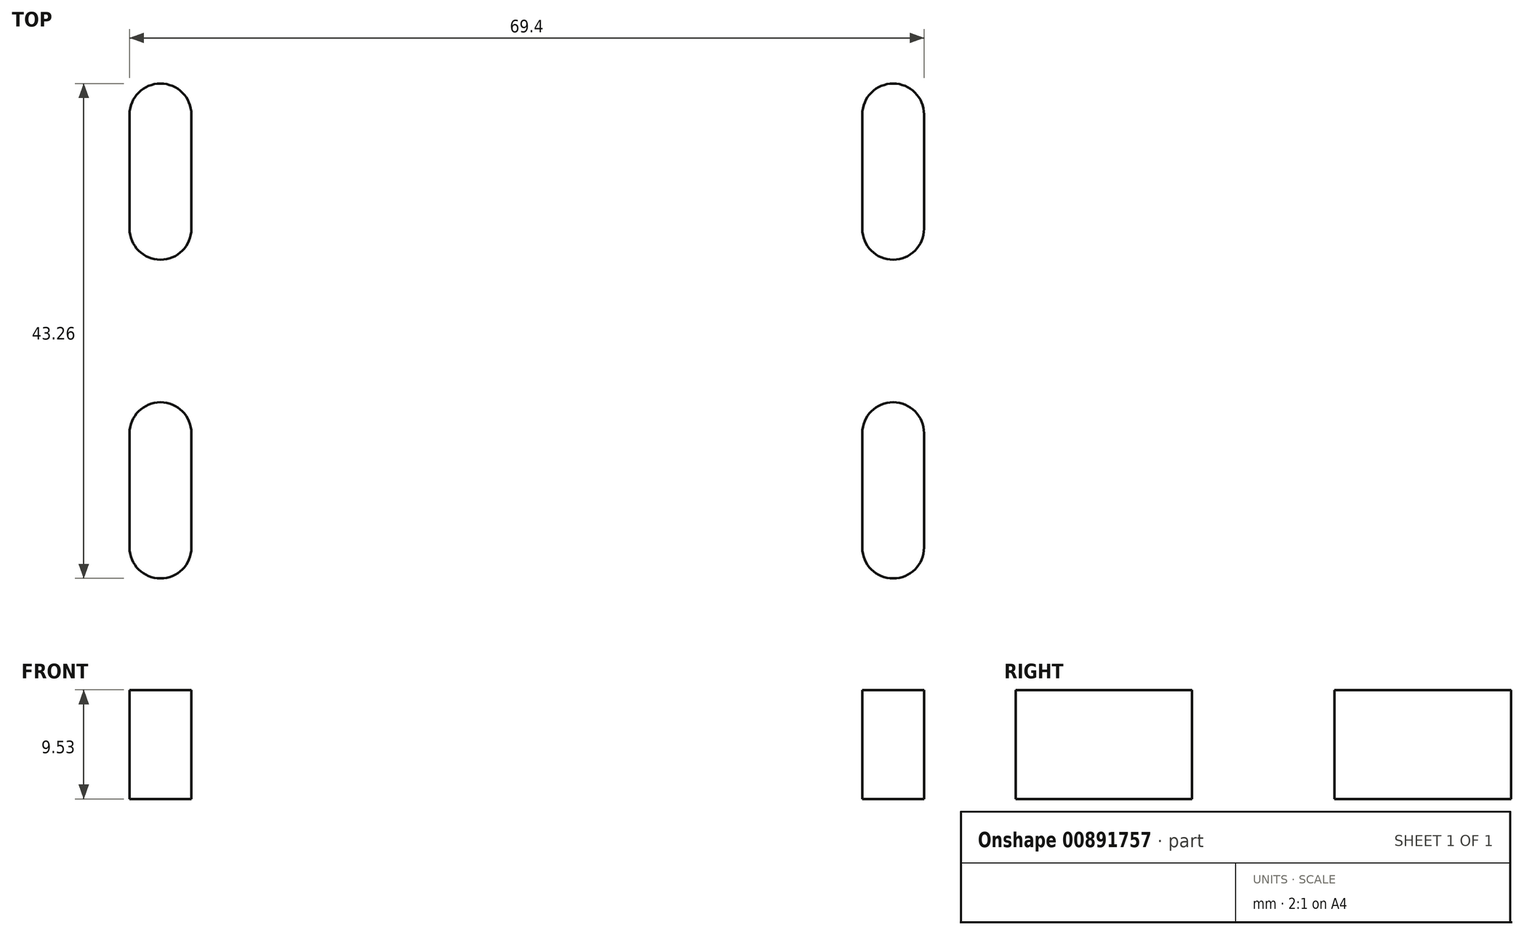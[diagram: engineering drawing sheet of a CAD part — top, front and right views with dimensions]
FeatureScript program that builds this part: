
annotation { "Feature Type Name" : "Feature", "Feature Type Description" : "" }
export const myFeature = defineFeature(function(context is Context, id is Id, definition is map)
    precondition{}
    {
        {
            var Q0;
            Q0=qCreatedBy(makeId("Top.planeOp"),FACE);
            var sketch = newSketch(context, id + "F0", { "sketchPlane" : qUnion([Q0])});
            skLineSegment(sketch, "E0.bottom", {"start": v(40, -25) * mm, "end": v(-40, -25) * mm});
            skLineSegment(sketch, "E0.top", {"start": v(40, 25) * mm, "end": v(-40, 25) * mm});
            skLineSegment(sketch, "E0.left", {"start": v(40, -25) * mm, "end": v(40, 25) * mm});
            skLineSegment(sketch, "E0.right", {"start": v(-40, -25) * mm, "end": v(-40, 25) * mm});
            skPoint(sketch, "E0.middle", {"position": v(0, 0) * mm});
            skSolve(sketch);
        }
        {
            var Q0;
            Q0=makeQuery(id+"F0.imprint","IMPRINT",FACE,{"disambiguationData":[TD([[makeQuery(id+"F0.imprint","IMPRINT",EDGE,{"derivedFrom":sQuery(id+"F0.wireOp",EDGE,"E0.bottom")}),-1.0]])]});
            extrude(context, id + "F1", {"entities" : qUnion([Q0]), "depth" : 9.52 * mm, "offsetDistance" : 25 * mm});
        }
        {
            var Q0;
            Q0=makeQuery(id+"F1.opExtrude","CAP_FACE",FACE,{"disambiguationData":[OSD([sQuery(id+"F0.wireOp",EDGE,"E0.bottom"),sQuery(id+"F0.wireOp",EDGE,"E0.top"),sQuery(id+"F0.wireOp",EDGE,"E0.left"),sQuery(id+"F0.wireOp",EDGE,"E0.right")])],"isStart":true});
            var sketch = newSketch(context, id + "F2", { "sketchPlane" : qUnion([Q0])});
            skPoint(sketch, "E1", {"position": v(-15, 12.3) * mm});
            skPoint(sketch, "E2.MirrorP", {"position": v(15, 12.3) * mm});
            skSolve(sketch);
        }
        {
            var Q0;
            Q0=makeQuery(id+"F1.opExtrude","CAP_FACE",FACE,{"disambiguationData":[OSD([sQuery(id+"F0.wireOp",EDGE,"E0.bottom"),sQuery(id+"F0.wireOp",EDGE,"E0.top"),sQuery(id+"F0.wireOp",EDGE,"E0.left"),sQuery(id+"F0.wireOp",EDGE,"E0.right")])],"isStart":false});
            var sketch = newSketch(context, id + "F3", { "sketchPlane" : qUnion([Q0])});
            skLineSegment(sketch, "E3", {"start": v(-32, 18.93) * mm, "end": v(-32, 8.93) * mm});
            skLineSegment(sketch, "E4.MirrorCS", {"start": v(32, 18.93) * mm, "end": v(32, 8.93) * mm});
            skLineSegment(sketch, "E5.MirrorCS", {"start": v(-32, -18.93) * mm, "end": v(-32, -8.93) * mm});
            skLineSegment(sketch, "E6.MirrorCS", {"start": v(32, -18.93) * mm, "end": v(32, -8.93) * mm});
            skArc(sketch, "E7.0.startCap", {"start": v(-34.7, 18.93) * mm, "mid": v(-32, 21.63) * mm, "end": v(-29.3, 18.93) * mm});
            skArc(sketch, "E7.0.endCap", {"start": v(-29.3, 8.93) * mm, "mid": v(-32, 6.23) * mm, "end": v(-34.7, 8.93) * mm});
            skLineSegment(sketch, "E7.0.left", {"start": v(-29.3, 18.93) * mm, "end": v(-29.3, 8.93) * mm});
            skLineSegment(sketch, "E7.0.right", {"start": v(-34.7, 18.93) * mm, "end": v(-34.7, 8.93) * mm});
            skArc(sketch, "E8.0.startCap", {"start": v(29.3, 18.93) * mm, "mid": v(32, 21.63) * mm, "end": v(34.7, 18.93) * mm});
            skArc(sketch, "E8.0.endCap", {"start": v(34.7, 8.93) * mm, "mid": v(32, 6.23) * mm, "end": v(29.3, 8.93) * mm});
            skLineSegment(sketch, "E8.0.left", {"start": v(34.7, 18.93) * mm, "end": v(34.7, 8.93) * mm});
            skLineSegment(sketch, "E8.0.right", {"start": v(29.3, 18.93) * mm, "end": v(29.3, 8.93) * mm});
            skArc(sketch, "E8.1.startCap", {"start": v(34.7, -18.93) * mm, "mid": v(32, -21.63) * mm, "end": v(29.3, -18.93) * mm});
            skArc(sketch, "E8.1.endCap", {"start": v(29.3, -8.93) * mm, "mid": v(32, -6.23) * mm, "end": v(34.7, -8.93) * mm});
            skLineSegment(sketch, "E8.1.left", {"start": v(29.3, -18.93) * mm, "end": v(29.3, -8.93) * mm});
            skLineSegment(sketch, "E8.1.right", {"start": v(34.7, -18.93) * mm, "end": v(34.7, -8.93) * mm});
            skArc(sketch, "E8.2.startCap", {"start": v(-29.3, -18.93) * mm, "mid": v(-32, -21.63) * mm, "end": v(-34.7, -18.93) * mm});
            skArc(sketch, "E8.2.endCap", {"start": v(-34.7, -8.93) * mm, "mid": v(-32, -6.23) * mm, "end": v(-29.3, -8.93) * mm});
            skLineSegment(sketch, "E8.2.left", {"start": v(-34.7, -18.93) * mm, "end": v(-34.7, -8.93) * mm});
            skLineSegment(sketch, "E8.2.right", {"start": v(-29.3, -18.93) * mm, "end": v(-29.3, -8.93) * mm});
            skSolve(sketch);
        }
        {
            var Q0;
            Q0=makeQuery(id+"F3.imprint","IMPRINT",FACE,{"disambiguationData":[TD([[makeQuery(id+"F3.imprint","IMPRINT",EDGE,{"derivedFrom":sQuery(id+"F3.wireOp",EDGE,"E7.0.startCap")}),-1.0]])]});
            var Q1;
            Q1=makeQuery(id+"F3.imprint","IMPRINT",FACE,{"disambiguationData":[TD([[makeQuery(id+"F3.imprint","IMPRINT",EDGE,{"derivedFrom":sQuery(id+"F3.wireOp",EDGE,"E8.2.startCap")}),-1.0]])]});
            var Q2;
            Q2=makeQuery(id+"F3.imprint","IMPRINT",FACE,{"disambiguationData":[TD([[makeQuery(id+"F3.imprint","IMPRINT",EDGE,{"derivedFrom":sQuery(id+"F3.wireOp",EDGE,"E8.1.startCap")}),-1.0]])]});
            var Q3;
            Q3=makeQuery(id+"F3.imprint","IMPRINT",FACE,{"disambiguationData":[TD([[makeQuery(id+"F3.imprint","IMPRINT",EDGE,{"derivedFrom":sQuery(id+"F3.wireOp",EDGE,"E8.0.startCap")}),-1.0]])]});
            extrude(context, id + "F4", {"entities" : qUnion([Q0, Q1, Q2, Q3]), "operationType" : NewBodyOperationType.REMOVE, "oppositeDirection" : true, "depth" : 25 * mm, "offsetDistance" : 25 * mm});
        }
        {
            var Q0;
            Q0=makeQuery(id+"F1.opExtrude","CAP_FACE",FACE,{"disambiguationData":[OSD([sQuery(id+"F0.wireOp",EDGE,"E0.bottom"),sQuery(id+"F0.wireOp",EDGE,"E0.top"),sQuery(id+"F0.wireOp",EDGE,"E0.left"),sQuery(id+"F0.wireOp",EDGE,"E0.right")])],"isStart":false});
            var sketch = newSketch(context, id + "F5", { "sketchPlane" : qUnion([Q0])});
            skCircle(sketch, "E9", {"center": v(0, 4.68) * mm, "radius": 4.76 * mm});
            skSolve(sketch);
        }
        {
            var Q0;
            Q0=makeQuery(id+"F5.imprint","IMPRINT",FACE,{"disambiguationData":[TD([[makeQuery(id+"F5.imprint","IMPRINT",EDGE,{"derivedFrom":sQuery(id+"F5.wireOp",EDGE,"E9")}),1.0]])]});
            extrude(context, id + "F6", {"entities" : qUnion([Q0]), "operationType" : NewBodyOperationType.REMOVE, "endBound" : BoundingType.THROUGH_ALL, "oppositeDirection" : true, "depth" : 25 * mm, "offsetDistance" : 25 * mm});
        }
        {
            var Q0;
            Q0=sQuery(id+"F2.wireOp",VERTEX,"E1");
            var Q1;
            Q1=sQuery(id+"F2.wireOp",VERTEX,"E2.MirrorP");
            var Q2;
            Q2=makeQuery(id+"F1.opExtrude","SWEPT_BODY",BODY,{"disambiguationData":[OSD([sQuery(id+"F0.wireOp",EDGE,"E0.bottom"),sQuery(id+"F0.wireOp",EDGE,"E0.top"),sQuery(id+"F0.wireOp",EDGE,"E0.left"),sQuery(id+"F0.wireOp",EDGE,"E0.right")])]});
            hole(context, id + "F7", {"style" : HoleStyle.C_BORE, "endStyle" : HoleEndStyle.THROUGH, "standardTappedOrClearance" : lookupTablePath({ "fit" : "Normal", "standard" : "ISO", "size" : "M5", "type" : "Clearance" }), "standardBlindInLast" : lookupTablePath({ "fit" : "Normal", "standard" : "ISO", "size" : "M5", "type" : "Clearance" }), "holeDiameter" : 5.5 * mm, "cBoreDiameter" : 9.75 * mm, "cBoreDepth" : 5 * mm, "majorDiameter" : 5 * mm, "isTappedThrough" : true, "tappedDepth" : 7.9 * mm, "tapClearance" : 3, "startFromSketch" : true, "locations" : qUnion([Q0, Q1]), "scope" : qUnion([Q2])});
        }
    });
